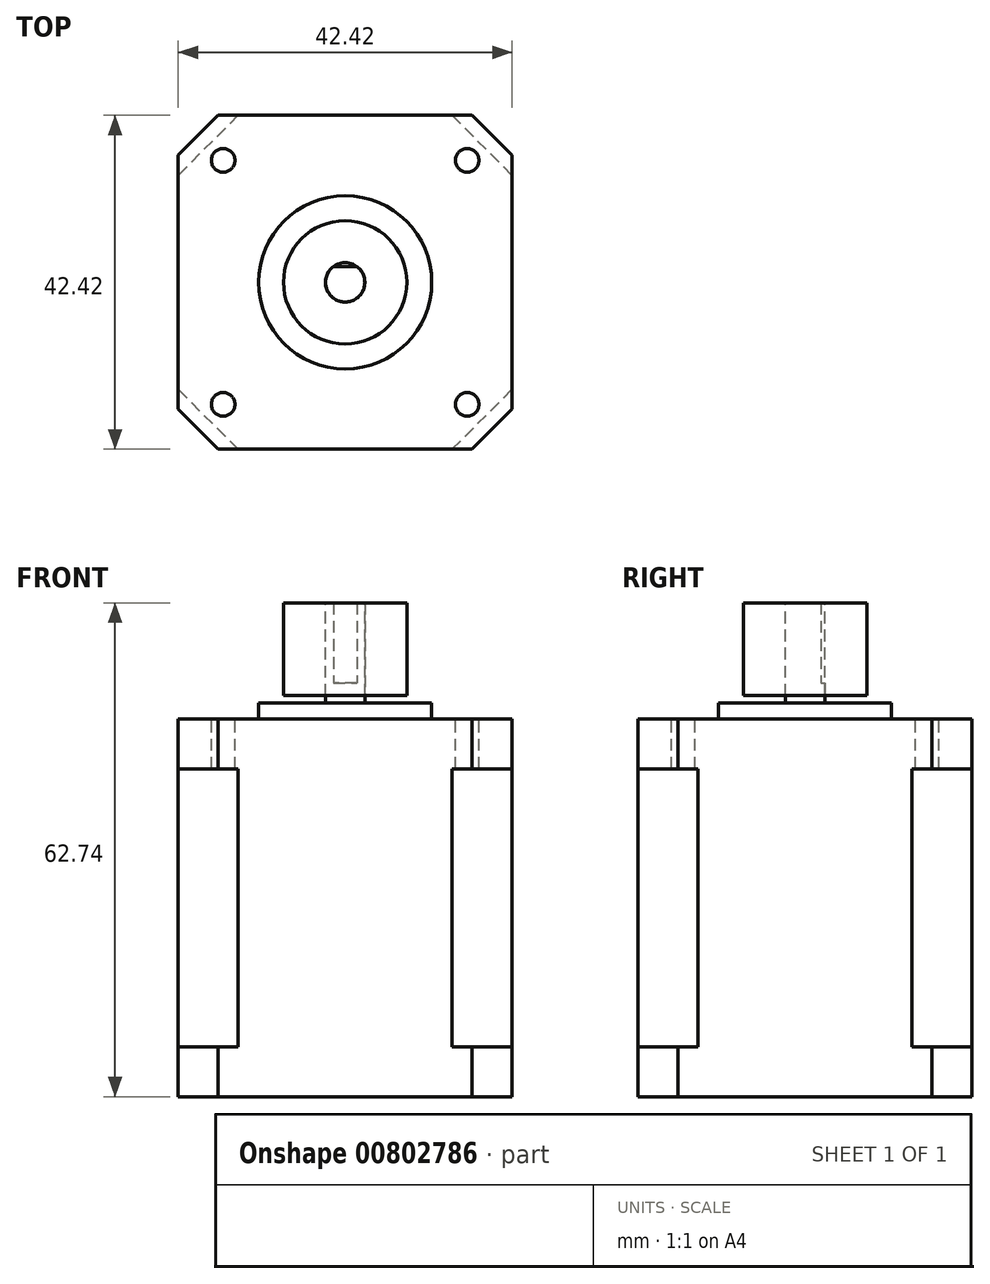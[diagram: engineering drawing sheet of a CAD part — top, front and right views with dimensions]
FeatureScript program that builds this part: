
annotation { "Feature Type Name" : "Feature", "Feature Type Description" : "" }
export const myFeature = defineFeature(function(context is Context, id is Id, definition is map)
    precondition{}
    {
        {
            var Q0;
            Q0=qCreatedBy(makeId("Top.planeOp"),FACE);
            var sketch = newSketch(context, id + "F0", { "sketchPlane" : qUnion([Q0])});
            skLineSegment(sketch, "E0.bottom", {"start": v(-21.2, 21.2) * mm, "end": v(21.2, 21.2) * mm});
            skLineSegment(sketch, "E0.top", {"start": v(-21.2, -21.2) * mm, "end": v(21.2, -21.2) * mm});
            skLineSegment(sketch, "E0.left", {"start": v(-21.2, 21.2) * mm, "end": v(-21.2, -21.2) * mm});
            skLineSegment(sketch, "E0.right", {"start": v(21.2, 21.2) * mm, "end": v(21.2, -21.2) * mm});
            skSolve(sketch);
        }
        {
            var Q0;
            Q0=makeQuery(id+"F0.imprint","IMPRINT",FACE,{"disambiguationData":[TD([[makeQuery(id+"F0.imprint","IMPRINT",EDGE,{"derivedFrom":sQuery(id+"F0.wireOp",EDGE,"E0.bottom")}),-1.0]])]});
            extrude(context, id + "F1", {"entities" : qUnion([Q0]), "endBound" : BoundingType.SYMMETRIC, "depth" : 35.3 * mm});
        }
        {
            var Q0;
            Q0=makeQuery(id+"F1.opExtrude","SWEPT_EDGE",EDGE,{"disambiguationData":[OSD([sQuery(id+"F0.wireOp",EDGE,"E0.bottom"),sQuery(id+"F0.wireOp",EDGE,"E0.right")])]});
            var Q1;
            Q1=makeQuery(id+"F1.opExtrude","SWEPT_EDGE",EDGE,{"disambiguationData":[OSD([sQuery(id+"F0.wireOp",EDGE,"E0.bottom"),sQuery(id+"F0.wireOp",EDGE,"E0.left")])]});
            var Q2;
            Q2=makeQuery(id+"F1.opExtrude","SWEPT_EDGE",EDGE,{"disambiguationData":[OSD([sQuery(id+"F0.wireOp",EDGE,"E0.top"),sQuery(id+"F0.wireOp",EDGE,"E0.left")])]});
            var Q3;
            Q3=makeQuery(id+"F1.opExtrude","SWEPT_EDGE",EDGE,{"disambiguationData":[OSD([sQuery(id+"F0.wireOp",EDGE,"E0.top"),sQuery(id+"F0.wireOp",EDGE,"E0.right")])]});
            chamfer(context, id + "F2", {"entities" : qUnion([Q0, Q1, Q2, Q3]), "width" : 7.62 * mm, "tangentPropagation" : true});
        }
        {
            var Q0;
            Q0=makeQuery(id+"F1.opExtrude","CAP_FACE",FACE,{"disambiguationData":[OSD([sQuery(id+"F0.wireOp",EDGE,"E0.bottom"),sQuery(id+"F0.wireOp",EDGE,"E0.top"),sQuery(id+"F0.wireOp",EDGE,"E0.left"),sQuery(id+"F0.wireOp",EDGE,"E0.right")])],"isStart":false});
            var sketch = newSketch(context, id + "F3", { "sketchPlane" : qUnion([Q0])});
            skLineSegment(sketch, "E1.bottom", {"start": v(-21.2, 21.2) * mm, "end": v(21.2, 21.2) * mm});
            skLineSegment(sketch, "E1.top", {"start": v(-21.2, -21.2) * mm, "end": v(21.2, -21.2) * mm});
            skLineSegment(sketch, "E1.left", {"start": v(-21.2, 21.2) * mm, "end": v(-21.2, -21.2) * mm});
            skLineSegment(sketch, "E1.right", {"start": v(21.2, 21.2) * mm, "end": v(21.2, -21.2) * mm});
            skSolve(sketch);
        }
        {
            var Q0;
            {var subQ0=sQuery(id+"F0.wireOp",EDGE,"E0.top");var subQ1=sQuery(id+"F0.wireOp",EDGE,"E0.right");var subQ2=sQuery(id+"F0.wireOp",EDGE,"E0.bottom");var subQ3=sQuery(id+"F0.wireOp",EDGE,"E0.left");var subQ4=makeQuery(id+"F1.opExtrude","CAP_FACE",FACE,{"disambiguationData":[OSD([subQ2,subQ0,subQ3,subQ1])],"isStart":false});var subQ8=makeQuery(id+"F2.opChamfer","BLEND_EDGE",EDGE,{"blendedFrom":[makeQuery(id+"F1.opExtrude","SWEPT_EDGE",EDGE,{"disambiguationData":[OSD([subQ2,subQ3])]}),subQ4],"blendedInto":[subQ4]});Q0=makeQuery(id+"F3.imprint","IMPRINT",FACE,{"disambiguationData":[TD([[makeQuery(id+"F3.imprint","IMPRINT",EDGE,{"derivedFrom":subQ8}),1.0]])]});}
            var Q1;
            {var subQ0=sQuery(id+"F0.wireOp",EDGE,"E0.bottom");var subQ1=sQuery(id+"F0.wireOp",EDGE,"E0.right");var subQ2=makeQuery(id+"F2.opChamfer","BLEND_EDGE",EDGE,{"blendedFrom":[makeQuery(id+"F1.opExtrude","SWEPT_EDGE",EDGE,{"disambiguationData":[OSD([subQ0,subQ1])]}),makeQuery(id+"F1.opExtrude","CAP_FACE",FACE,{"disambiguationData":[OSD([subQ0,sQuery(id+"F0.wireOp",EDGE,"E0.top"),sQuery(id+"F0.wireOp",EDGE,"E0.left"),subQ1])],"isStart":false})],"blendedInto":[makeQuery(id+"F1.opExtrude","CAP_FACE",FACE,{"disambiguationData":[OSD([subQ0,sQuery(id+"F0.wireOp",EDGE,"E0.top"),sQuery(id+"F0.wireOp",EDGE,"E0.left"),subQ1])],"isStart":false})]});Q1=makeQuery(id+"F3.imprint","IMPRINT",FACE,{"disambiguationData":[TD([[makeQuery(id+"F3.imprint","IMPRINT",EDGE,{"derivedFrom":subQ2}),-1.0]])]});}
            var Q2;
            {var subQ0=sQuery(id+"F0.wireOp",EDGE,"E0.bottom");var subQ1=sQuery(id+"F0.wireOp",EDGE,"E0.left");var subQ2=makeQuery(id+"F2.opChamfer","BLEND_EDGE",EDGE,{"blendedFrom":[makeQuery(id+"F1.opExtrude","SWEPT_EDGE",EDGE,{"disambiguationData":[OSD([subQ0,subQ1])]}),makeQuery(id+"F1.opExtrude","CAP_FACE",FACE,{"disambiguationData":[OSD([subQ0,sQuery(id+"F0.wireOp",EDGE,"E0.top"),subQ1,sQuery(id+"F0.wireOp",EDGE,"E0.right")])],"isStart":false})],"blendedInto":[makeQuery(id+"F1.opExtrude","CAP_FACE",FACE,{"disambiguationData":[OSD([subQ0,sQuery(id+"F0.wireOp",EDGE,"E0.top"),subQ1,sQuery(id+"F0.wireOp",EDGE,"E0.right")])],"isStart":false})]});Q2=makeQuery(id+"F3.imprint","IMPRINT",FACE,{"disambiguationData":[TD([[makeQuery(id+"F3.imprint","IMPRINT",EDGE,{"derivedFrom":subQ2}),-1.0]])]});}
            var Q3;
            {var subQ0=sQuery(id+"F0.wireOp",EDGE,"E0.top");var subQ1=sQuery(id+"F0.wireOp",EDGE,"E0.left");var subQ2=makeQuery(id+"F2.opChamfer","BLEND_EDGE",EDGE,{"blendedFrom":[makeQuery(id+"F1.opExtrude","SWEPT_EDGE",EDGE,{"disambiguationData":[OSD([subQ0,subQ1])]}),makeQuery(id+"F1.opExtrude","CAP_FACE",FACE,{"disambiguationData":[OSD([sQuery(id+"F0.wireOp",EDGE,"E0.bottom"),subQ0,subQ1,sQuery(id+"F0.wireOp",EDGE,"E0.right")])],"isStart":false})],"blendedInto":[makeQuery(id+"F1.opExtrude","CAP_FACE",FACE,{"disambiguationData":[OSD([sQuery(id+"F0.wireOp",EDGE,"E0.bottom"),subQ0,subQ1,sQuery(id+"F0.wireOp",EDGE,"E0.right")])],"isStart":false})]});Q3=makeQuery(id+"F3.imprint","IMPRINT",FACE,{"disambiguationData":[TD([[makeQuery(id+"F3.imprint","IMPRINT",EDGE,{"derivedFrom":subQ2}),-1.0]])]});}
            var Q4;
            {var subQ0=sQuery(id+"F0.wireOp",EDGE,"E0.top");var subQ1=sQuery(id+"F0.wireOp",EDGE,"E0.right");var subQ2=makeQuery(id+"F2.opChamfer","BLEND_EDGE",EDGE,{"blendedFrom":[makeQuery(id+"F1.opExtrude","SWEPT_EDGE",EDGE,{"disambiguationData":[OSD([subQ0,subQ1])]}),makeQuery(id+"F1.opExtrude","CAP_FACE",FACE,{"disambiguationData":[OSD([sQuery(id+"F0.wireOp",EDGE,"E0.bottom"),subQ0,sQuery(id+"F0.wireOp",EDGE,"E0.left"),subQ1])],"isStart":false})],"blendedInto":[makeQuery(id+"F1.opExtrude","CAP_FACE",FACE,{"disambiguationData":[OSD([sQuery(id+"F0.wireOp",EDGE,"E0.bottom"),subQ0,sQuery(id+"F0.wireOp",EDGE,"E0.left"),subQ1])],"isStart":false})]});Q4=makeQuery(id+"F3.imprint","IMPRINT",FACE,{"disambiguationData":[TD([[makeQuery(id+"F3.imprint","IMPRINT",EDGE,{"derivedFrom":subQ2}),-1.0]])]});}
            extrude(context, id + "F4", {"entities" : qUnion([Q0, Q1, Q2, Q3, Q4]), "operationType" : NewBodyOperationType.ADD, "depth" : 6.35 * mm});
        }
        {
            var Q0;
            Q0=makeQuery(id+"F4.opExtrude","SWEPT_EDGE",EDGE,{"disambiguationData":[OSD([sQuery(id+"F3.wireOp",EDGE,"E1.bottom"),sQuery(id+"F3.wireOp",EDGE,"E1.right")])]});
            var Q1;
            Q1=makeQuery(id+"F4.opExtrude","SWEPT_EDGE",EDGE,{"disambiguationData":[OSD([sQuery(id+"F3.wireOp",EDGE,"E1.bottom"),sQuery(id+"F3.wireOp",EDGE,"E1.left")])]});
            var Q2;
            Q2=makeQuery(id+"F4.opExtrude","SWEPT_EDGE",EDGE,{"disambiguationData":[OSD([sQuery(id+"F3.wireOp",EDGE,"E1.top"),sQuery(id+"F3.wireOp",EDGE,"E1.left")])]});
            var Q3;
            Q3=makeQuery(id+"F4.opExtrude","SWEPT_EDGE",EDGE,{"disambiguationData":[OSD([sQuery(id+"F3.wireOp",EDGE,"E1.top"),sQuery(id+"F3.wireOp",EDGE,"E1.right")])]});
            chamfer(context, id + "F5", {"entities" : qUnion([Q0, Q1, Q2, Q3]), "width" : 5.08 * mm, "tangentPropagation" : true});
        }
        {
            var Q0;
            Q0=makeQuery(id+"F1.opExtrude","CAP_FACE",FACE,{"disambiguationData":[OSD([sQuery(id+"F0.wireOp",EDGE,"E0.bottom"),sQuery(id+"F0.wireOp",EDGE,"E0.top"),sQuery(id+"F0.wireOp",EDGE,"E0.left"),sQuery(id+"F0.wireOp",EDGE,"E0.right")])],"isStart":true});
            var sketch = newSketch(context, id + "F6", { "sketchPlane" : qUnion([Q0])});
            skLineSegment(sketch, "E2.0.0", {"start": v(-16.13, 21.2) * mm, "end": v(16.13, 21.2) * mm});
            skLineSegment(sketch, "E2.0.1", {"start": v(16.13, 21.2) * mm, "end": v(21.2, 16.13) * mm});
            skLineSegment(sketch, "E2.0.2", {"start": v(21.2, -16.13) * mm, "end": v(21.2, 16.13) * mm});
            skLineSegment(sketch, "E2.0.3", {"start": v(21.2, -16.13) * mm, "end": v(16.13, -21.2) * mm});
            skLineSegment(sketch, "E2.0.4", {"start": v(-16.13, -21.2) * mm, "end": v(16.13, -21.2) * mm});
            skLineSegment(sketch, "E2.0.5", {"start": v(-16.13, -21.2) * mm, "end": v(-21.2, -16.13) * mm});
            skLineSegment(sketch, "E2.0.6", {"start": v(-21.2, -16.13) * mm, "end": v(-21.2, 16.13) * mm});
            skLineSegment(sketch, "E2.0.7", {"start": v(-21.2, 16.13) * mm, "end": v(-16.13, 21.2) * mm});
            skSolve(sketch);
        }
        {
            var Q0;
            {var subQ3=sQuery(id+"F6.wireOp",EDGE,"E2.0.7");Q0=makeQuery(id+"F6.imprint","IMPRINT",FACE,{"disambiguationData":[TD([[makeQuery(id+"F6.imprint","IMPRINT",EDGE,{"derivedFrom":subQ3}),-1.0]])]});}
            var Q1;
            {var subQ4=sQuery(id+"F6.wireOp",EDGE,"E2.0.1");Q1=makeQuery(id+"F6.imprint","IMPRINT",FACE,{"disambiguationData":[TD([[makeQuery(id+"F6.imprint","IMPRINT",EDGE,{"derivedFrom":subQ4}),-1.0]])]});}
            var Q2;
            {var subQ4=sQuery(id+"F6.wireOp",EDGE,"E2.0.3");Q2=makeQuery(id+"F6.imprint","IMPRINT",FACE,{"disambiguationData":[TD([[makeQuery(id+"F6.imprint","IMPRINT",EDGE,{"derivedFrom":subQ4}),-1.0]])]});}
            var Q3;
            {var subQ4=sQuery(id+"F6.wireOp",EDGE,"E2.0.5");Q3=makeQuery(id+"F6.imprint","IMPRINT",FACE,{"disambiguationData":[TD([[makeQuery(id+"F6.imprint","IMPRINT",EDGE,{"derivedFrom":subQ4}),-1.0]])]});}
            var Q4;
            {var subQ0=sQuery(id+"F0.wireOp",EDGE,"E0.top");var subQ1=sQuery(id+"F0.wireOp",EDGE,"E0.right");var subQ2=sQuery(id+"F0.wireOp",EDGE,"E0.bottom");var subQ3=sQuery(id+"F0.wireOp",EDGE,"E0.left");var subQ4=makeQuery(id+"F1.opExtrude","CAP_FACE",FACE,{"disambiguationData":[OSD([subQ2,subQ0,subQ3,subQ1])],"isStart":true});var subQ8=makeQuery(id+"F2.opChamfer","BLEND_EDGE",EDGE,{"blendedFrom":[makeQuery(id+"F1.opExtrude","SWEPT_EDGE",EDGE,{"disambiguationData":[OSD([subQ2,subQ3])]}),subQ4],"blendedInto":[subQ4]});Q4=makeQuery(id+"F6.imprint","IMPRINT",FACE,{"disambiguationData":[TD([[makeQuery(id+"F6.imprint","IMPRINT",EDGE,{"derivedFrom":subQ8}),1.0]])]});}
            extrude(context, id + "F7", {"entities" : qUnion([Q0, Q1, Q2, Q3, Q4]), "operationType" : NewBodyOperationType.ADD, "depth" : 6.35 * mm});
        }
        {
            var Q0;
            Q0=makeQuery(id+"F4.opExtrude","CAP_FACE",FACE,{"disambiguationData":[OSD([sQuery(id+"F3.wireOp",EDGE,"E1.bottom"),sQuery(id+"F3.wireOp",EDGE,"E1.top"),sQuery(id+"F3.wireOp",EDGE,"E1.left"),sQuery(id+"F3.wireOp",EDGE,"E1.right")])],"isStart":false});
            var sketch = newSketch(context, id + "F8", { "sketchPlane" : qUnion([Q0])});
            skCircle(sketch, "E3", {"center": v(0, 0) * mm, "radius": 11 * mm});
            skSolve(sketch);
        }
        {
            var Q0;
            Q0=makeQuery(id+"F8.imprint","IMPRINT",FACE,{"disambiguationData":[TD([[makeQuery(id+"F8.imprint","IMPRINT",EDGE,{"derivedFrom":sQuery(id+"F8.wireOp",EDGE,"E3")}),1.0]])]});
            extrude(context, id + "F9", {"entities" : qUnion([Q0]), "operationType" : NewBodyOperationType.ADD, "depth" : 2.03 * mm});
        }
        {
            var Q0;
            Q0=makeQuery(id+"F9.opExtrude","CAP_FACE",FACE,{"disambiguationData":[OSD([sQuery(id+"F8.wireOp",EDGE,"E3")])],"isStart":false});
            var sketch = newSketch(context, id + "F10", { "sketchPlane" : qUnion([Q0])});
            skCircle(sketch, "E4", {"center": v(0, 0) * mm, "radius": 2.5 * mm});
            skSolve(sketch);
        }
        {
            var Q0;
            Q0=makeQuery(id+"F10.imprint","IMPRINT",FACE,{"disambiguationData":[TD([[makeQuery(id+"F10.imprint","IMPRINT",EDGE,{"derivedFrom":sQuery(id+"F10.wireOp",EDGE,"E4")}),1.0]])]});
            extrude(context, id + "F11", {"entities" : qUnion([Q0]), "operationType" : NewBodyOperationType.ADD, "depth" : 12.7 * mm});
        }
        {
            var Q0;
            Q0=makeQuery(id+"F11.opExtrude","CAP_FACE",FACE,{"disambiguationData":[OSD([sQuery(id+"F10.wireOp",EDGE,"E4")])],"isStart":false});
            var sketch = newSketch(context, id + "F12", { "sketchPlane" : qUnion([Q0])});
            skLineSegment(sketch, "E5.bottom", {"start": v(-2.63, 2.93) * mm, "end": v(2.62, 2.93) * mm});
            skLineSegment(sketch, "E5.top", {"start": v(-2.63, 2) * mm, "end": v(2.62, 2) * mm});
            skLineSegment(sketch, "E5.left", {"start": v(-2.63, 2.93) * mm, "end": v(-2.63, 2) * mm});
            skLineSegment(sketch, "E5.right", {"start": v(2.62, 2.93) * mm, "end": v(2.62, 2) * mm});
            skSolve(sketch);
        }
        {
            var Q0;
            {var subQ0=makeQuery(id+"F11.opExtrude","CAP_EDGE",EDGE,{"disambiguationData":[OSD([sQuery(id+"F10.wireOp",EDGE,"E4")])],"isStart":false});var subQ1=sQuery(id+"F12.wireOp",EDGE,"E5.top");var subQ3=makeQuery(id+"F12.imprint","INTERSECT",VERTEX,{"disambiguationData":[OD(0.0)],"derivedFrom":[subQ0,subQ1]});Q0=qUnion([makeQuery(id+"F12.imprint","IMPRINT",FACE,{"disambiguationData":[TD([[makeQuery(id+"F12.imprint","IMPRINT",EDGE,{"derivedFrom":sQuery(id+"F12.wireOp",EDGE,"E5.bottom")}),-1.0]])]}),makeQuery(id+"F12.imprint","IMPRINT",FACE,{"disambiguationData":[TD([[makeQuery(id+"F12.imprint","IMPRINT",EDGE,{"disambiguationData":[TD([[subQ3,-1.0]])],"derivedFrom":subQ1}),1.0]])]})]);}
            extrude(context, id + "F13", {"entities" : qUnion([Q0]), "operationType" : NewBodyOperationType.REMOVE, "oppositeDirection" : true, "depth" : 10.16 * mm});
        }
        {
            var Q0;
            Q0=makeQuery(id+"F4.opExtrude","CAP_FACE",FACE,{"disambiguationData":[OSD([sQuery(id+"F3.wireOp",EDGE,"E1.bottom"),sQuery(id+"F3.wireOp",EDGE,"E1.top"),sQuery(id+"F3.wireOp",EDGE,"E1.left"),sQuery(id+"F3.wireOp",EDGE,"E1.right")])],"isStart":false});
            var sketch = newSketch(context, id + "F14", { "sketchPlane" : qUnion([Q0])});
            skLineSegment(sketch, "E6.rect.bottom", {"start": v(15.5, 15.5) * mm, "end": v(-15.5, 15.5) * mm, "construction": true});
            skLineSegment(sketch, "E6.rect.top", {"start": v(15.5, -15.5) * mm, "end": v(-15.5, -15.5) * mm, "construction": true});
            skLineSegment(sketch, "E6.rect.left", {"start": v(15.5, 15.5) * mm, "end": v(15.5, -15.5) * mm, "construction": true});
            skLineSegment(sketch, "E6.rect.right", {"start": v(-15.5, 15.5) * mm, "end": v(-15.5, -15.5) * mm, "construction": true});
            skPoint(sketch, "E6.rect.middle", {"position": v(0, 0) * mm});
            skCircle(sketch, "E7", {"center": v(-15.5, 15.5) * mm, "radius": 1.5 * mm});
            skCircle(sketch, "E8", {"center": v(15.5, 15.5) * mm, "radius": 1.5 * mm});
            skCircle(sketch, "E9", {"center": v(15.5, -15.5) * mm, "radius": 1.5 * mm});
            skCircle(sketch, "E10", {"center": v(-15.5, -15.5) * mm, "radius": 1.5 * mm});
            skSolve(sketch);
        }
        {
            var Q0;
            Q0=makeQuery(id+"F14.imprint","IMPRINT",FACE,{"disambiguationData":[TD([[makeQuery(id+"F14.imprint","IMPRINT",EDGE,{"derivedFrom":sQuery(id+"F14.wireOp",EDGE,"E7")}),1.0]])]});
            var Q1;
            Q1=makeQuery(id+"F14.imprint","IMPRINT",FACE,{"disambiguationData":[TD([[makeQuery(id+"F14.imprint","IMPRINT",EDGE,{"derivedFrom":sQuery(id+"F14.wireOp",EDGE,"E8")}),1.0]])]});
            var Q2;
            Q2=makeQuery(id+"F14.imprint","IMPRINT",FACE,{"disambiguationData":[TD([[makeQuery(id+"F14.imprint","IMPRINT",EDGE,{"derivedFrom":sQuery(id+"F14.wireOp",EDGE,"E9")}),1.0]])]});
            var Q3;
            Q3=makeQuery(id+"F14.imprint","IMPRINT",FACE,{"disambiguationData":[TD([[makeQuery(id+"F14.imprint","IMPRINT",EDGE,{"derivedFrom":sQuery(id+"F14.wireOp",EDGE,"E10")}),1.0]])]});
            extrude(context, id + "F15", {"entities" : qUnion([Q0, Q1, Q2, Q3]), "operationType" : NewBodyOperationType.REMOVE, "oppositeDirection" : true, "depth" : 6.35 * mm});
        }
        {
            var Q0;
            Q0=makeQuery(id+"F11.opExtrude","CAP_FACE",FACE,{"disambiguationData":[OSD([sQuery(id+"F10.wireOp",EDGE,"E4")])],"isStart":false});
            var sketch = newSketch(context, id + "F16", { "sketchPlane" : qUnion([Q0])});
            skCircle(sketch, "E11", {"center": v(0, 0) * mm, "radius": 7.83 * mm});
            skCircle(sketch, "E12", {"center": v(0, 0) * mm, "radius": 2.5 * mm});
            skSolve(sketch);
        }
        {
            var Q0;
            Q0=makeQuery(id+"F16.imprint","IMPRINT",FACE,{"disambiguationData":[TD([[makeQuery(id+"F16.imprint","IMPRINT",EDGE,{"derivedFrom":sQuery(id+"F16.wireOp",EDGE,"E11")}),1.0]])]});
            extrude(context, id + "F17", {"entities" : qUnion([Q0]), "oppositeDirection" : true, "depth" : 11.8 * mm});
        }
    });
